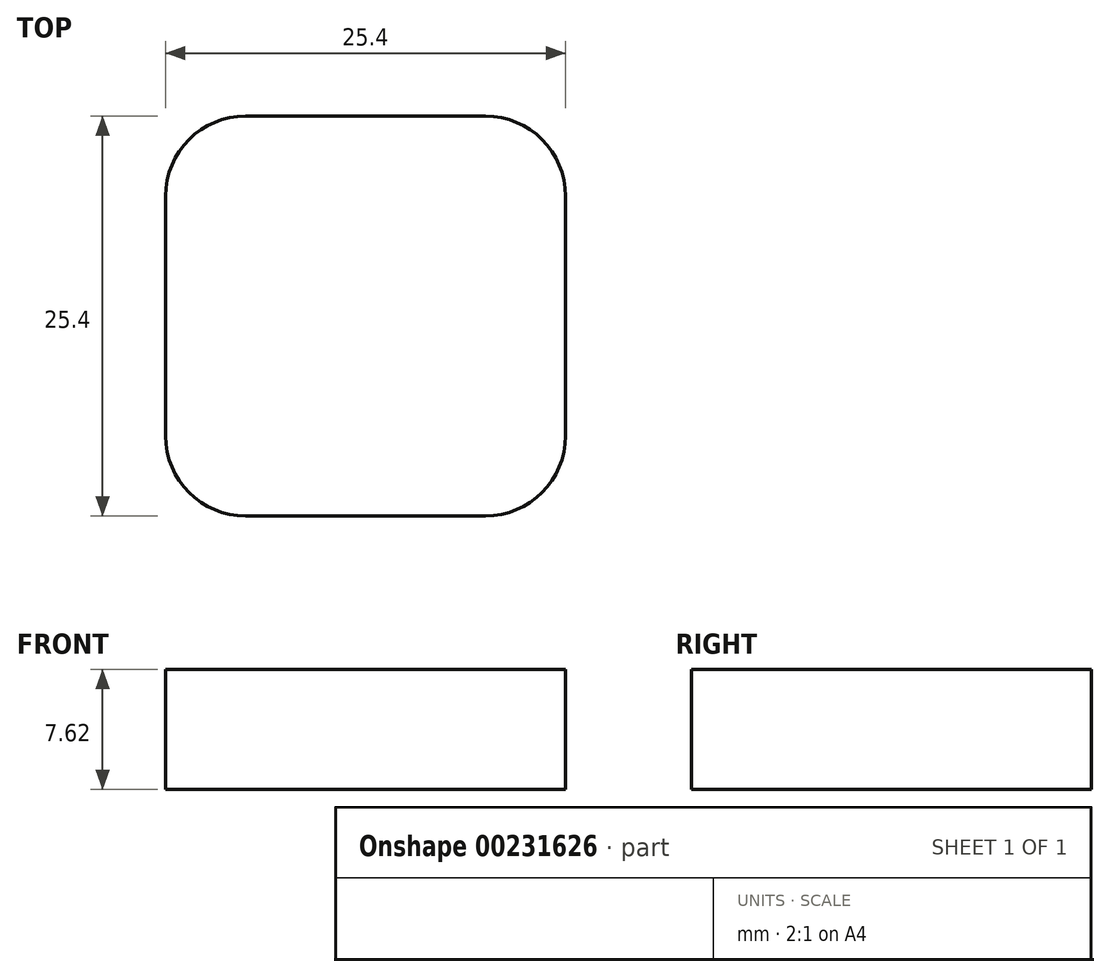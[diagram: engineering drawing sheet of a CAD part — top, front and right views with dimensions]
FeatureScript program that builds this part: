
annotation { "Feature Type Name" : "Feature", "Feature Type Description" : "" }
export const myFeature = defineFeature(function(context is Context, id is Id, definition is map)
    precondition{}
    {
        {
            var Q0;
            Q0=qCreatedBy(makeId("Top.planeOp"),FACE);
            var sketch = newSketch(context, id + "F0", { "sketchPlane" : qUnion([Q0])});
            skLineSegment(sketch, "E0.bottom", {"start": v(0, 0) * mm, "end": v(25.4, 0) * mm});
            skLineSegment(sketch, "E0.top", {"start": v(0, 25.4) * mm, "end": v(25.4, 25.4) * mm});
            skLineSegment(sketch, "E0.left", {"start": v(0, 0) * mm, "end": v(0, 25.4) * mm});
            skLineSegment(sketch, "E0.right", {"start": v(25.4, 0) * mm, "end": v(25.4, 25.4) * mm});
            skSolve(sketch);
        }
        {
            var Q0;
            Q0=makeQuery(id+"F0.imprint","IMPRINT",FACE,{"disambiguationData":[TD([[makeQuery(id+"F0.imprint","IMPRINT",EDGE,{"derivedFrom":sQuery(id+"F0.wireOp",EDGE,"E0.bottom")}),1.0]])]});
            extrude(context, id + "F1", {"entities" : qUnion([Q0]), "depth" : 7.62 * mm});
        }
        {
            var Q0;
            Q0=makeQuery(id+"F1.opExtrude","SWEPT_EDGE",EDGE,{"disambiguationData":[OSD([sQuery(id+"F0.wireOp",EDGE,"E0.bottom"),sQuery(id+"F0.wireOp",EDGE,"E0.right")])]});
            var Q1;
            Q1=makeQuery(id+"F1.opExtrude","SWEPT_EDGE",EDGE,{"disambiguationData":[OSD([sQuery(id+"F0.wireOp",EDGE,"E0.top"),sQuery(id+"F0.wireOp",EDGE,"E0.right")])]});
            var Q2;
            Q2=makeQuery(id+"F1.opExtrude","SWEPT_EDGE",EDGE,{"disambiguationData":[OSD([sQuery(id+"F0.wireOp",EDGE,"E0.top"),sQuery(id+"F0.wireOp",EDGE,"E0.left")])]});
            var Q3;
            Q3=makeQuery(id+"F1.opExtrude","SWEPT_EDGE",EDGE,{"disambiguationData":[OSD([sQuery(id+"F0.wireOp",EDGE,"E0.bottom"),sQuery(id+"F0.wireOp",EDGE,"E0.left")])]});
            fillet(context, id + "F2", {"entities" : qUnion([Q0, Q1, Q2, Q3]), "radius" : 5.08 * mm, "tangentPropagation" : true, "allowEdgeOverflow" : false});
        }
    });
